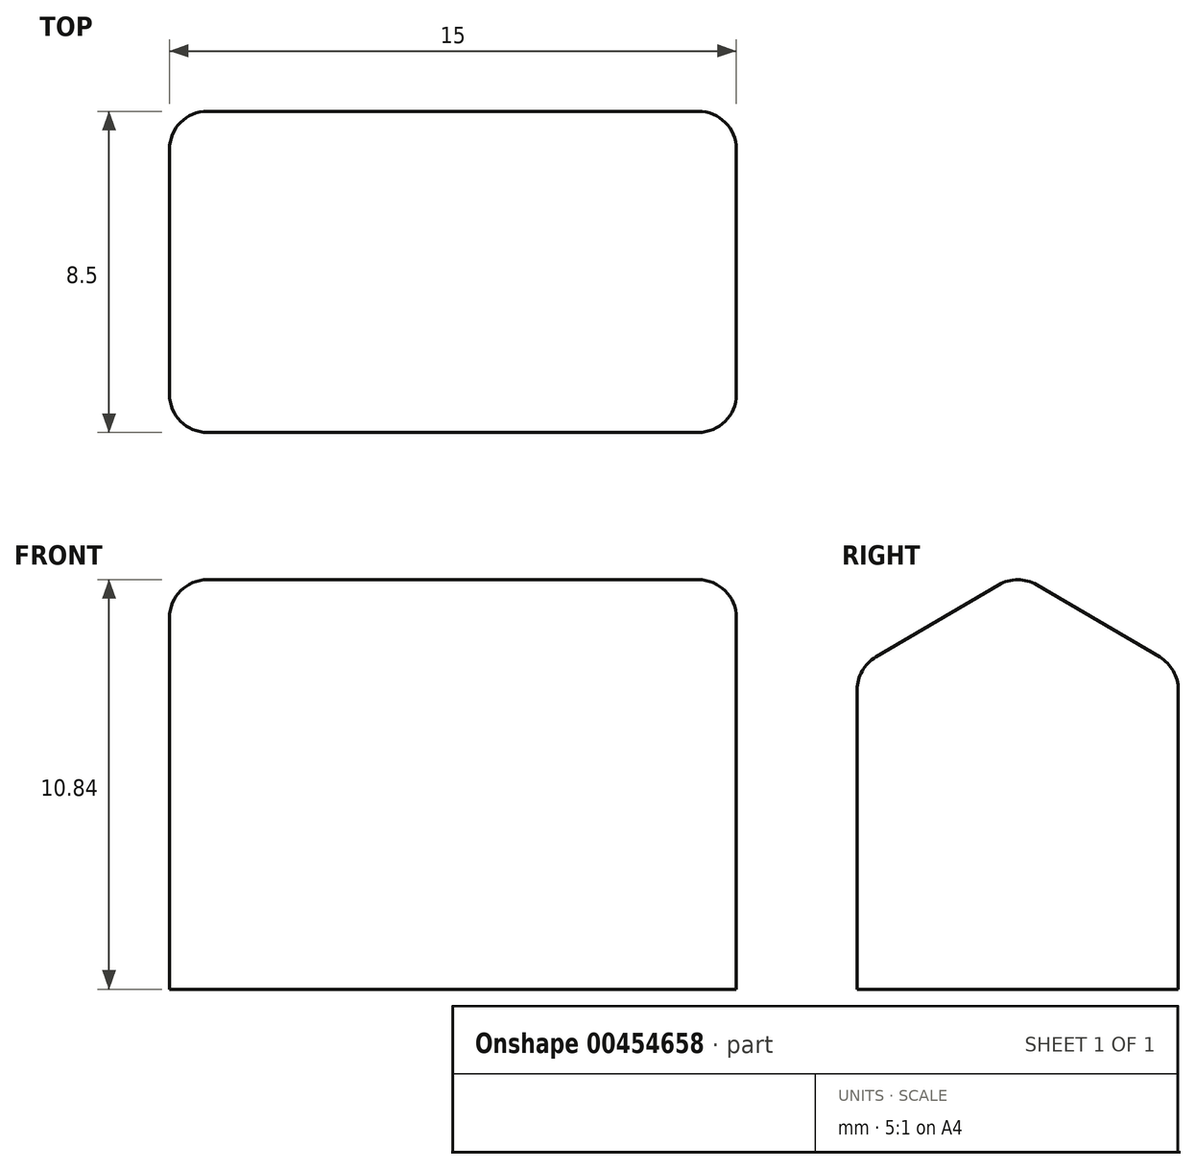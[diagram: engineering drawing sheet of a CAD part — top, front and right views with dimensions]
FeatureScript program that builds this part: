
annotation { "Feature Type Name" : "Feature", "Feature Type Description" : "" }
export const myFeature = defineFeature(function(context is Context, id is Id, definition is map)
    precondition{}
    {
        {
            var Q0;
            Q0=qCreatedBy(makeId("Right.planeOp"),FACE);
            var sketch = newSketch(context, id + "F0", { "sketchPlane" : qUnion([Q0])});
            skLineSegment(sketch, "E0.bottom", {"start": v(-4.25, 0) * mm, "end": v(0, 0) * mm});
            skLineSegment(sketch, "E0.top", {"start": v(-4.25, 8.5) * mm, "end": v(0, 8.5) * mm, "construction": true});
            skLineSegment(sketch, "E0.left", {"start": v(-4.25, 0) * mm, "end": v(-4.25, 8.5) * mm});
            skLineSegment(sketch, "E0.right", {"start": v(0, 0) * mm, "end": v(0, 8.5) * mm, "construction": true});
            skPoint(sketch, "E1", {"position": v(0, 11) * mm});
            skLineSegment(sketch, "E2", {"start": v(-4.25, 8.5) * mm, "end": v(0, 11) * mm});
            skLineSegment(sketch, "E3.MirrorCS", {"start": v(4.25, 8.5) * mm, "end": v(0, 11) * mm});
            skLineSegment(sketch, "E4.MirrorCS", {"start": v(4.25, 0) * mm, "end": v(4.25, 8.5) * mm});
            skLineSegment(sketch, "E5.MirrorCS", {"start": v(4.25, 0) * mm, "end": v(0, 0) * mm});
            skSolve(sketch);
        }
        {
            var Q0;
            Q0 = qSketchRegion(id + "F0", true);
            extrude(context, id + "F1", {"entities" : qUnion([Q0]), "depth" : 15 * mm, "offsetDistance" : 25 * mm});
        }
        {
            var Q0;
            Q0=makeQuery(id+"F1.opExtrude","SWEPT_EDGE",EDGE,{"disambiguationData":[OSD([sQuery(id+"F0.wireOp",EDGE,"E0.left"),sQuery(id+"F0.wireOp",EDGE,"E2")])]});
            var Q1;
            Q1=makeQuery(id+"F1.opExtrude","SWEPT_EDGE",EDGE,{"disambiguationData":[OSD([sQuery(id+"F0.wireOp",EDGE,"E2"),sQuery(id+"F0.wireOp",EDGE,"E3.MirrorCS")])]});
            var Q2;
            Q2=makeQuery(id+"F1.opExtrude","SWEPT_EDGE",EDGE,{"disambiguationData":[OSD([sQuery(id+"F0.wireOp",EDGE,"E3.MirrorCS"),sQuery(id+"F0.wireOp",EDGE,"E4.MirrorCS")])]});
            var Q3;
            Q3=makeQuery(id+"F1.opExtrude","CAP_EDGE",EDGE,{"disambiguationData":[OSD([sQuery(id+"F0.wireOp",EDGE,"E3.MirrorCS")])],"isStart":false});
            var Q4;
            Q4=makeQuery(id+"F1.opExtrude","CAP_EDGE",EDGE,{"disambiguationData":[OSD([sQuery(id+"F0.wireOp",EDGE,"E2")])],"isStart":false});
            var Q5;
            Q5=makeQuery(id+"F1.opExtrude","CAP_EDGE",EDGE,{"disambiguationData":[OSD([sQuery(id+"F0.wireOp",EDGE,"E3.MirrorCS")])],"isStart":true});
            var Q6;
            Q6=makeQuery(id+"F1.opExtrude","CAP_EDGE",EDGE,{"disambiguationData":[OSD([sQuery(id+"F0.wireOp",EDGE,"E2")])],"isStart":true});
            var Q7;
            Q7=makeQuery(id+"F1.opExtrude","CAP_EDGE",EDGE,{"disambiguationData":[OSD([sQuery(id+"F0.wireOp",EDGE,"E0.left")])],"isStart":true});
            var Q8;
            Q8=makeQuery(id+"F1.opExtrude","CAP_EDGE",EDGE,{"disambiguationData":[OSD([sQuery(id+"F0.wireOp",EDGE,"E4.MirrorCS")])],"isStart":true});
            var Q9;
            Q9=makeQuery(id+"F1.opExtrude","CAP_EDGE",EDGE,{"disambiguationData":[OSD([sQuery(id+"F0.wireOp",EDGE,"E0.left")])],"isStart":false});
            var Q10;
            Q10=makeQuery(id+"F1.opExtrude","CAP_EDGE",EDGE,{"disambiguationData":[OSD([sQuery(id+"F0.wireOp",EDGE,"E4.MirrorCS")])],"isStart":false});
            fillet(context, id + "F2", {"entities" : qUnion([Q0, Q1, Q2, Q3, Q4, Q5, Q6, Q7, Q8, Q9, Q10]), "tangentPropagation" : true, "radius" : 1 * mm, "defaultsChanged" : false, "vertexSettings" : [], "allowEdgeOverflow" : false});
        }
    });
